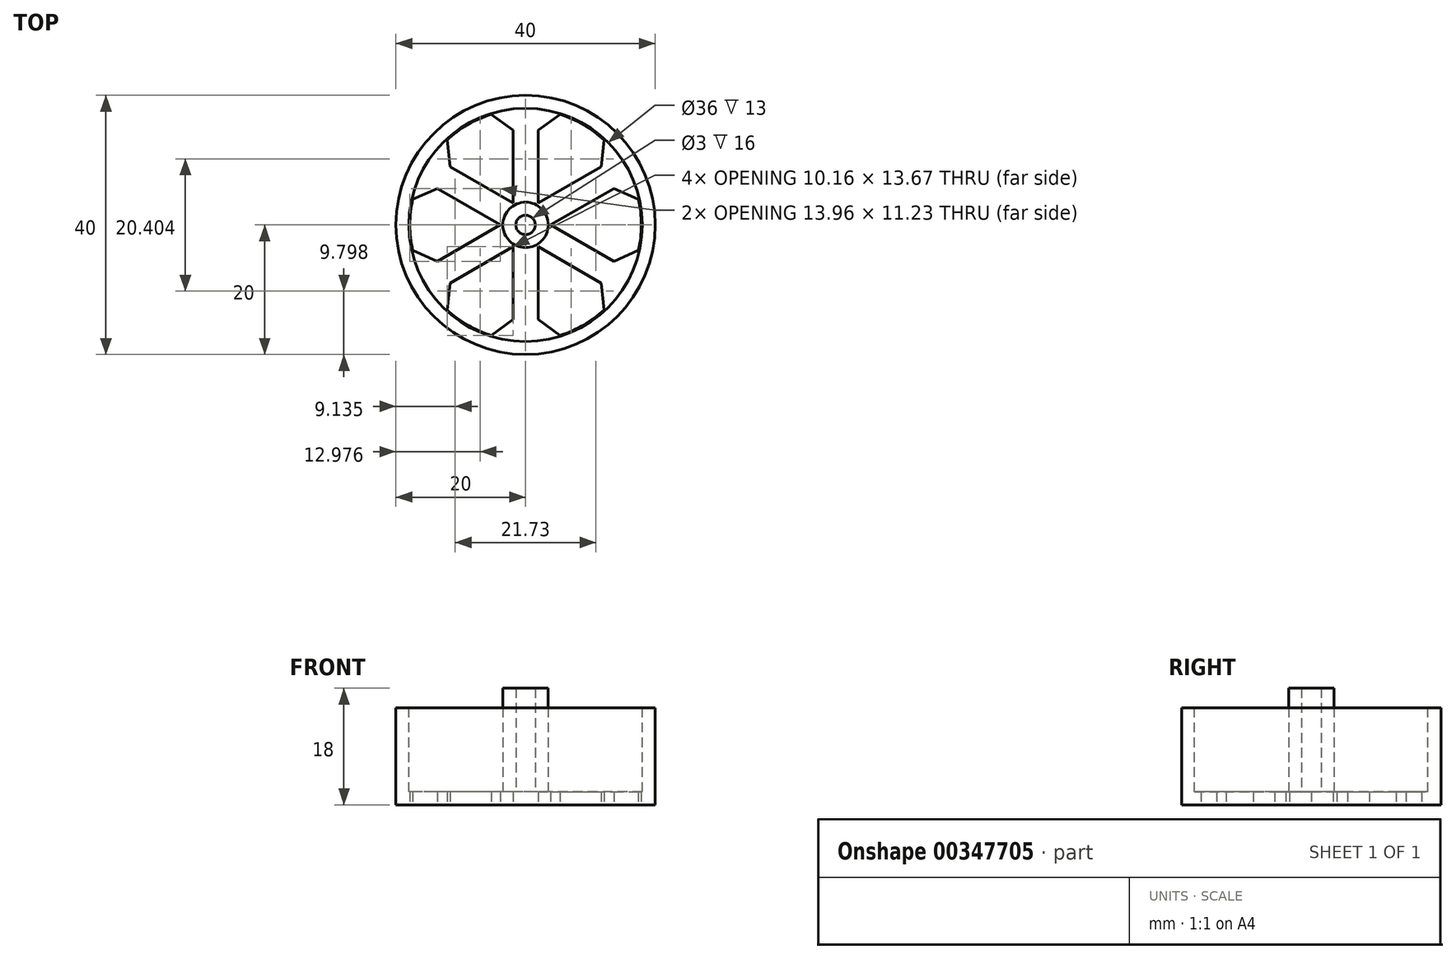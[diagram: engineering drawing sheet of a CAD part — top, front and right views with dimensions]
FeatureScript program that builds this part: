
annotation { "Feature Type Name" : "Feature", "Feature Type Description" : "" }
export const myFeature = defineFeature(function(context is Context, id is Id, definition is map)
    precondition{}
    {
        {
            var Q0;
            Q0=qCreatedBy(makeId("Top.planeOp"),FACE);
            var sketch = newSketch(context, id + "F0", { "sketchPlane" : qUnion([Q0])});
            skCircle(sketch, "E0", {"center": v(0, 0) * mm, "radius": 20 * mm});
            skSolve(sketch);
        }
        {
            var Q0;
            Q0=makeQuery(id+"F0.imprint","IMPRINT",FACE,{"disambiguationData":[TD([[makeQuery(id+"F0.imprint","IMPRINT",EDGE,{"derivedFrom":sQuery(id+"F0.wireOp",EDGE,"E0")}),1.0]])]});
            extrude(context, id + "F1", {"entities" : qUnion([Q0]), "depth" : 15 * mm});
        }
        {
            var Q0;
            Q0=makeQuery(id+"F1.opExtrude","CAP_FACE",FACE,{"disambiguationData":[OSD([sQuery(id+"F0.wireOp",EDGE,"E0")])],"isStart":false});
            var sketch = newSketch(context, id + "F2", { "sketchPlane" : qUnion([Q0])});
            skCircle(sketch, "E1", {"center": v(0, 0) * mm, "radius": 18 * mm});
            skSolve(sketch);
        }
        {
            var Q0;
            Q0=makeQuery(id+"F2.imprint","IMPRINT",FACE,{"disambiguationData":[TD([[makeQuery(id+"F2.imprint","IMPRINT",EDGE,{"derivedFrom":sQuery(id+"F2.wireOp",EDGE,"E1")}),1.0]])]});
            extrude(context, id + "F3", {"entities" : qUnion([Q0]), "operationType" : NewBodyOperationType.REMOVE, "oppositeDirection" : true, "depth" : 13 * mm});
        }
        {
            var Q0;
            Q0=makeQuery(id+"F3.boolean.opBoolean","COPY",FACE,{"derivedFrom":makeQuery(id+"F3.opExtrude","CAP_FACE",FACE,{"disambiguationData":[OSD([sQuery(id+"F2.wireOp",EDGE,"E1")])],"isStart":false})});
            var sketch = newSketch(context, id + "F4", { "sketchPlane" : qUnion([Q0])});
            skCircle(sketch, "E2", {"center": v(0, 0) * mm, "radius": 1.5 * mm});
            skCircle(sketch, "E3", {"center": v(0, 0) * mm, "radius": 3.5 * mm});
            skSolve(sketch);
        }
        {
            var Q0;
            Q0=makeQuery(id+"F4.imprint","IMPRINT",FACE,{"disambiguationData":[TD([[makeQuery(id+"F4.imprint","IMPRINT",EDGE,{"derivedFrom":sQuery(id+"F4.wireOp",EDGE,"E2")}),-1.0]])]});
            extrude(context, id + "F5", {"entities" : qUnion([Q0]), "operationType" : NewBodyOperationType.ADD, "depth" : 16 * mm});
        }
        {
            var Q0;
            Q0=qCreatedBy(makeId("Top.planeOp"),FACE);
            var sketch = newSketch(context, id + "F6", { "sketchPlane" : qUnion([Q0])});
            skLineSegment(sketch, "E4", {"start": v(-1.94, 3.14) * mm, "end": v(-1.94, 14.6) * mm});
            skLineSegment(sketch, "E5.MirrorCS", {"start": v(1.94, 3.14) * mm, "end": v(1.94, 14.6) * mm});
            skLineSegment(sketch, "E6", {"start": v(1.94, 14.6) * mm, "end": v(5.3, 17.04) * mm});
            skLineSegment(sketch, "E7.MirrorCS", {"start": v(-1.94, 14.6) * mm, "end": v(-5.3, 17.04) * mm});
            skLineSegment(sketch, "E8.MirrorCS", {"start": v(-1.94, -3.14) * mm, "end": v(-1.94, -14.6) * mm});
            skLineSegment(sketch, "E9.MirrorCS", {"start": v(1.94, -3.14) * mm, "end": v(1.94, -14.6) * mm});
            skLineSegment(sketch, "E10.1.0", {"start": v(-1.75, 3.25) * mm, "end": v(-11.67, 8.98) * mm});
            skLineSegment(sketch, "E10.2.0", {"start": v(-3.7, 0.11) * mm, "end": v(-13.61, -5.62) * mm});
            skLineSegment(sketch, "E10.4.0", {"start": v(1.75, -3.25) * mm, "end": v(11.67, -8.98) * mm});
            skLineSegment(sketch, "E10.5.0", {"start": v(3.7, -0.11) * mm, "end": v(13.61, 5.62) * mm});
            skPoint(sketch, "E10.center", {"position": v(0, 0) * mm});
            skLineSegment(sketch, "E11.MirrorCS", {"start": v(1.75, 3.25) * mm, "end": v(11.67, 8.98) * mm});
            skLineSegment(sketch, "E12.MirrorCS", {"start": v(3.7, 0.11) * mm, "end": v(13.61, -5.62) * mm});
            skLineSegment(sketch, "E13.MirrorCS", {"start": v(-1.75, -3.25) * mm, "end": v(-11.67, -8.98) * mm});
            skLineSegment(sketch, "E14.MirrorCS", {"start": v(-3.7, -0.11) * mm, "end": v(-13.61, 5.62) * mm});
            skLineSegment(sketch, "E15.1.0", {"start": v(-13.61, 5.62) * mm, "end": v(-17.4, 3.93) * mm});
            skLineSegment(sketch, "E15.1.1", {"start": v(-11.67, 8.98) * mm, "end": v(-12.1, 13.11) * mm});
            skLineSegment(sketch, "E15.2.0", {"start": v(-11.67, -8.98) * mm, "end": v(-12.1, -13.11) * mm});
            skLineSegment(sketch, "E15.2.1", {"start": v(-13.61, -5.62) * mm, "end": v(-17.4, -3.93) * mm});
            skLineSegment(sketch, "E15.3.0", {"start": v(1.94, -14.6) * mm, "end": v(5.3, -17.04) * mm});
            skLineSegment(sketch, "E15.3.1", {"start": v(-1.94, -14.6) * mm, "end": v(-5.3, -17.04) * mm});
            skLineSegment(sketch, "E15.4.0", {"start": v(13.61, -5.62) * mm, "end": v(17.4, -3.93) * mm});
            skLineSegment(sketch, "E15.4.1", {"start": v(11.67, -8.98) * mm, "end": v(12.1, -13.11) * mm});
            skLineSegment(sketch, "E15.5.0", {"start": v(11.67, 8.98) * mm, "end": v(12.1, 13.11) * mm});
            skLineSegment(sketch, "E15.5.1", {"start": v(13.61, 5.62) * mm, "end": v(17.4, 3.93) * mm});
            skCircle(sketch, "E16", {"center": v(0, 0) * mm, "radius": 18 * mm});
            skCircle(sketch, "E17", {"center": v(0, 0) * mm, "radius": 17.84 * mm});
            skSolve(sketch);
        }
        {
            var Q0;
            {var subQ0=sQuery(id+"F6.wireOp",EDGE,"E15.1.0");Q0=makeQuery(id+"F6.imprint","IMPRINT",FACE,{"disambiguationData":[TD([[makeQuery(id+"F6.imprint","IMPRINT",EDGE,{"derivedFrom":subQ0}),1.0]])]});}
            var Q1;
            {var subQ0=sQuery(id+"F6.wireOp",EDGE,"E15.2.0");Q1=makeQuery(id+"F6.imprint","IMPRINT",FACE,{"disambiguationData":[TD([[makeQuery(id+"F6.imprint","IMPRINT",EDGE,{"derivedFrom":subQ0}),1.0]])]});}
            var Q2;
            {var subQ0=sQuery(id+"F6.wireOp",EDGE,"E15.3.0");Q2=makeQuery(id+"F6.imprint","IMPRINT",FACE,{"disambiguationData":[TD([[makeQuery(id+"F6.imprint","IMPRINT",EDGE,{"derivedFrom":subQ0}),1.0]])]});}
            var Q3;
            {var subQ1=sQuery(id+"F6.wireOp",EDGE,"E15.4.0");Q3=makeQuery(id+"F6.imprint","IMPRINT",FACE,{"disambiguationData":[TD([[makeQuery(id+"F6.imprint","IMPRINT",EDGE,{"derivedFrom":subQ1}),1.0]])]});}
            var Q4;
            {var subQ0=sQuery(id+"F6.wireOp",EDGE,"E6");Q4=makeQuery(id+"F6.imprint","IMPRINT",FACE,{"disambiguationData":[TD([[makeQuery(id+"F6.imprint","IMPRINT",EDGE,{"derivedFrom":subQ0}),-1.0]])]});}
            var Q5;
            {var subQ1=sQuery(id+"F6.wireOp",EDGE,"E7.MirrorCS");Q5=makeQuery(id+"F6.imprint","IMPRINT",FACE,{"disambiguationData":[TD([[makeQuery(id+"F6.imprint","IMPRINT",EDGE,{"derivedFrom":subQ1}),1.0]])]});}
            extrude(context, id + "F7", {"entities" : qUnion([Q0, Q1, Q2, Q3, Q4, Q5]), "operationType" : NewBodyOperationType.REMOVE, "depth" : 2 * mm});
        }
    });
